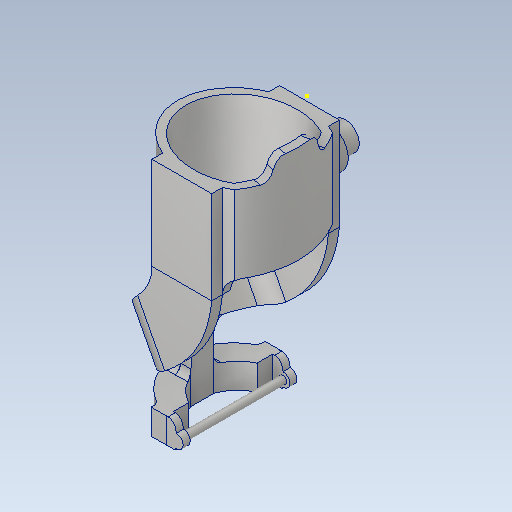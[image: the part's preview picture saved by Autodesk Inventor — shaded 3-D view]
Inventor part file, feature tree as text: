
AUTODESK INVENTOR PART (.ipt)
format: ipt  version: 2021 (Build 250183000, 183)  size: 1,478,144 bytes
history: native  units: in
note: dims shown in document units (in); Inventor stores cm internally (conversion verified against a paired STEP export)
features: sketch x30, extrude x14, fillet x11, plane x9, other x8, loft x5, mirror x4, revolve x2, direct_edit x2, sweep x1
ambient origin geometry x8: Origin, YZ Plane, XZ Plane, XY Plane, X Axis, Y Axis, Z Axis, Center Point
bodies: Solid1 (feature_tree)
feature tree (86):
  extrude  "Extrusion1"  Depth=11.4173in
  extrude  "Extrusion2"  Depth=2.8543in
  fillet  "Fillet1"  Radius=2.8543in
  sketch  "Sketch5"  dims[d8=5.7087in d10=1.1811in d11=1.1811in]
  sketch  "Sketch6"  dims[d12=150.0deg d13=60.0deg]
  plane  "Work Plane1"
  extrude  "Extrusion3"  Depth=1.1811in
  fillet  "Fillet2"  Radius=1.1811in
  extrude  "Extrusion4"  TaperAngle=60.0deg  [1 undecoded]
  extrude  "Extrusion5"  TaperAngle=60.0deg  [1 undecoded]
  fillet  "Fillet3"  Radius=6.063in
  plane  "Work Plane2"
  sketch  "Sketch12"  dims[d26=0.1768in d27=1.5748in d28=0.0in]
  plane  "Work Plane3"
  loft  "Loft1"
  plane  "Work Plane4"
  sketch  "Sketch16"  dims[d36=1.1811in d39=6.4259in d40=4.7244in]
  plane  "Work Plane5"
  loft  "Loft2"
  fillet  "Fillet4"  Radius=1.6828in
  fillet  "Fillet5"  Radius=6.063in
  fillet  "Fillet6"  Radius=1.1484in
  mirror  "Mirror1"
  loft  "Loft3"
  plane  "Work Plane6"
  loft  "Loft4"
  loft  "Loft5"
  fillet  "Fillet7"  Radius=0.7874in
  extrude  "Extrusion7"  Depth=1.1811in
  fillet  "Fillet8"  Radius=4.7244in
  extrude  "Extrusion9"  TaperAngle=0.0deg  [1 undecoded]
  mirror  "Mirror2"
  sketch  "Sketch25"  dims[d62=0.0in d63=90.0deg d64=-11.2598in]
  sketch  "Sketch27"  dims[d65=0.0in d66=90.0deg d67=0.0in d68=90.0deg]
  plane  "Work Plane8"
  sweep  "Sweep1"
  mirror  "Mirror3"
  plane  "Work Plane10"
  extrude  "Extrusion10"  Depth=1.1811in
  fillet  "Fillet10"  [1 undecoded]
  extrude  "Extrusion11"  TaperAngle=0.0deg  [1 undecoded]
  fillet  "Fillet11"  Radius=1.9685in
  extrude  "Extrusion12"  Depth=3.937in
  fillet  "Fillet12"  [1 undecoded]
  revolve  "Revolution3"  [1 undecoded]
  direct_edit  "Direct Edit1"
  direct_edit  "Direct Edit2"
  extrude  "Extrusion15"  TaperAngle=0.0deg  [1 undecoded]
  extrude  "Extrusion16"  Depth=0.9827in
  sketch  "Sketch39"  dims[d82=6.625in]
  sketch  "Sketch40"  dims[d83=1.9685in d84=0.0in]
  revolve  "Revolution4"  Angle=90.0deg
  sketch  "Sketch42"  dims[d91=1.9685in]
  plane  "Work Plane11"
  mirror  "Mirror5"
  extrude  "Extrusion18"  TaperAngle=60.0deg  [1 undecoded]
  extrude  "Extrusion19"  Depth=4.3341in
  sketch  "Sketch1"  dims[d0=12.9921in d1=11.4173in]
  sketch  "Sketch2"  dims[d4=5.7087in d5=2.8543in d7=2.8543in]
  sketch  "Sketch7"  dims[d14=150.0deg d15=60.0deg d16=6.063in d17=0.0in]
  sketch  "Sketch8"  dims[d18=1.1811in d19=0.0in d20=1.1811in]
  sketch  "Sketch9"  dims[d21=0.7946in d22=0.7946in d23=1.6828in d24=6.063in d25=1.1484in]
  sketch  "Sketch13"  dims[d29=1.1811in d30=2.3622in]
  sketch  "Sketch14"  dims[d31=0.7874in d32=0.0in d33=1.5748in d34=0.7874in d35=0.0in]
  sketch  "Sketch17"  dims[d41=1.1811in d42=0.0in d43=90.0deg]
  other  "Edges1"
  other  "Edges2"
  other  "Edges3"
  sketch  "Sketch18"  dims[d44=0.0in d45=90.0deg d46=0.0in d47=90.0deg]
  other  "Edges4"
  sketch  "Sketch19"  dims[d49=2.5591in d50=1.1811in d51=0.0in d52=90.0deg]
  other  "Edges5"
  sketch  "Sketch20"  dims[d53=0.0in d54=90.0deg d55=0.0in d56=90.0deg d57=1.9685in]
  sketch  "Sketch23"  dims[d58=1.9685in d59=3.937in d60=0.0in d61=90.0deg]
  sketch  "Sketch29"  dims[d69=2.5591in d70=0.9827in]
  sketch  "Sketch30"  dims[d71=0.0in d72=90.0deg d73=0.0in d74=90.0deg]
  sketch  "Sketch32"  dims[d75=1.1811in d76=60.0deg]
  sketch  "Sketch33"  dims[d77=120.0deg d78=4.3341in]
  sketch  "Sketch34"  dims[d79=6.625in]
  sketch  "Sketch37"  dims[d80=2.3604in]
  sketch  "Sketch38"  dims[d81=6.625in]
  sketch  "Sketch41"  dims[d85=0.5906in]
  sketch  "Sketch43"  dims[d92=0.7874in d93=1.7197in d94=0.9843in d95=0.0in d98=1.4173in d99=0.7874in d100=90.0deg d102=0.0in d103=0.0in d104=0.2362in d105=12.7711in d106=0.0in d107=0.7874in d108=1.9685in d109=0.0in d110=0.7874in d111=1.9685in d112=0.0in d113=0.7874in d114=180.0deg d115=0.2717in d116=0.3189in d117=0.2717in d124=0.2953in d125=0.3543in d126=0.2953in d127=0.4528in d128=0.3937in d129=0.3937in d130=2.3622in d131=1.0236in d132=0.0in d133=1.5748in d134=1.0236in d135=0.0in d137=270.0deg d138=0.4331in d141=6.7297in d142=0.0in d143=4.8586in d144=2.7237in d145=6.7297in d146=0.0in]
  other  "Scale1"
  other  "Scale2"
  other  "Scale3"
note: 9 required parameter values undecoded (feature->parameter linkage not recoverable at this tier; creation-order binding heuristic only, values carry confidence <= 0.55)